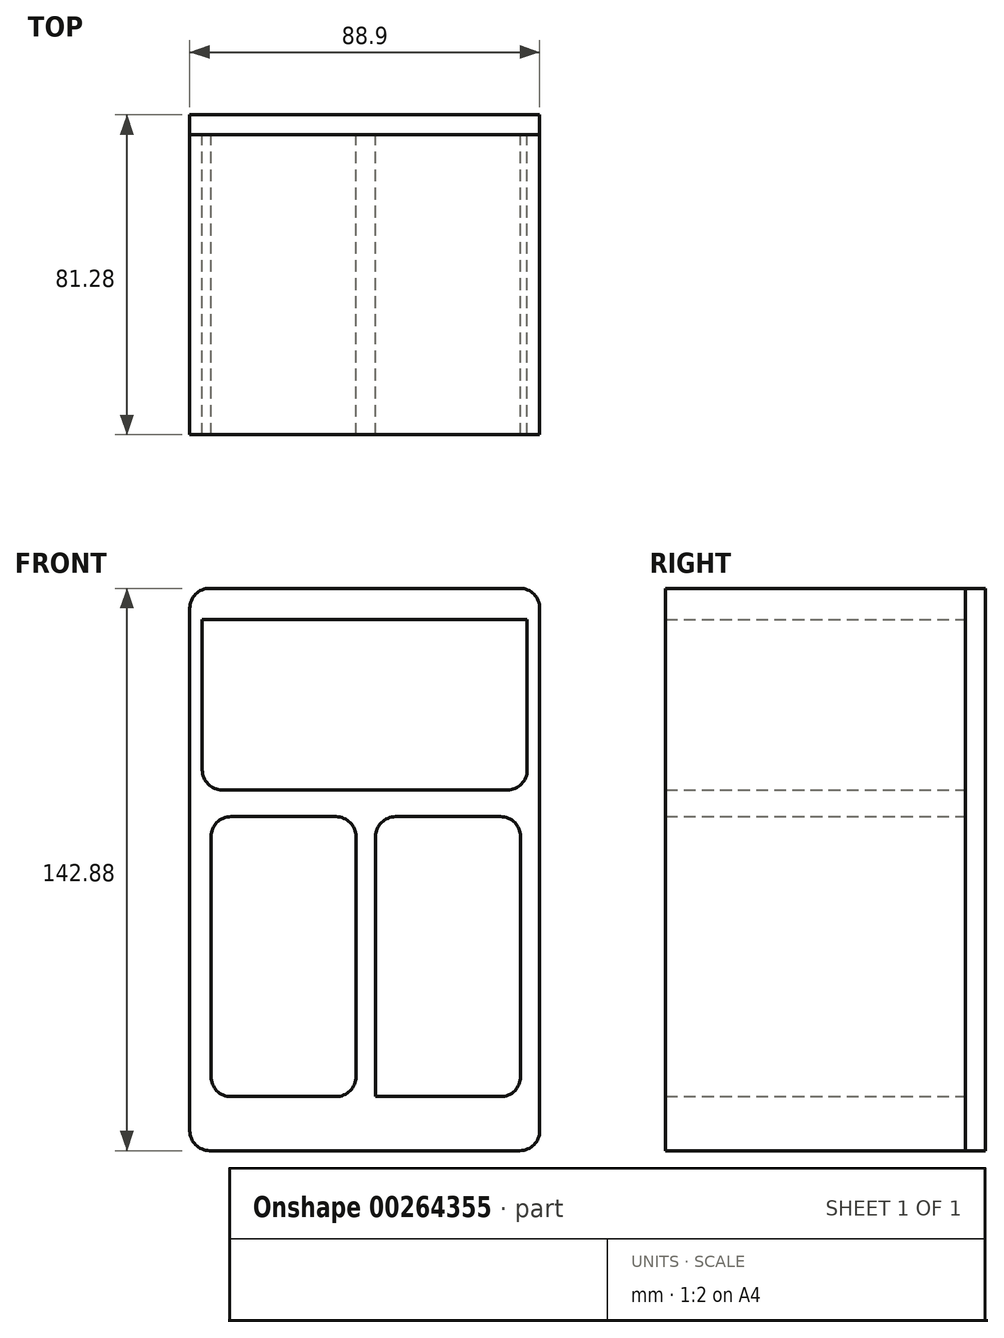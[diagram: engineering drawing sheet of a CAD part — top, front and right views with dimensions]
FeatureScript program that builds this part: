
annotation { "Feature Type Name" : "Feature", "Feature Type Description" : "" }
export const myFeature = defineFeature(function(context is Context, id is Id, definition is map)
    precondition{}
    {
        {
            var Q0;
            Q0=qCreatedBy(makeId("Front.planeOp"),FACE);
            var sketch = newSketch(context, id + "F0", { "sketchPlane" : qUnion([Q0])});
            skLineSegment(sketch, "E0.bottom", {"start": v(-44.45, 71.44) * mm, "end": v(44.45, 71.44) * mm});
            skLineSegment(sketch, "E0.top", {"start": v(-44.45, -71.44) * mm, "end": v(44.45, -71.44) * mm});
            skLineSegment(sketch, "E0.left", {"start": v(-44.45, 71.44) * mm, "end": v(-44.45, -71.44) * mm});
            skLineSegment(sketch, "E0.right", {"start": v(44.45, 71.44) * mm, "end": v(44.45, -71.44) * mm});
            skPoint(sketch, "E0.middle", {"position": v(0, 0) * mm});
            skLineSegment(sketch, "E1.bottom", {"start": v(-41.27, 63.5) * mm, "end": v(41.28, 63.5) * mm});
            skLineSegment(sketch, "E1.top", {"start": v(-41.28, -63.5) * mm, "end": v(41.27, -63.5) * mm});
            skLineSegment(sketch, "E1.left", {"start": v(-41.27, 63.5) * mm, "end": v(-41.28, -63.5) * mm});
            skLineSegment(sketch, "E1.right", {"start": v(41.28, 63.5) * mm, "end": v(41.27, -63.5) * mm});
            skLineSegment(sketch, "E2.bottom", {"start": v(-41.27, 63.5) * mm, "end": v(41.27, 63.5) * mm});
            skLineSegment(sketch, "E2.top", {"start": v(-41.27, 20.2) * mm, "end": v(41.27, 20.2) * mm});
            skLineSegment(sketch, "E2.left", {"start": v(-41.27, 63.5) * mm, "end": v(-41.27, 20.2) * mm});
            skLineSegment(sketch, "E2.right", {"start": v(41.27, 63.5) * mm, "end": v(41.27, 20.2) * mm});
            skPoint(sketch, "E2.middle", {"position": v(0, 41.85) * mm});
            skLineSegment(sketch, "E3.bottom", {"start": v(-39.08, 13.42) * mm, "end": v(-2.25, 13.42) * mm});
            skLineSegment(sketch, "E3.top", {"start": v(-39.08, -57.7) * mm, "end": v(-2.25, -57.7) * mm});
            skLineSegment(sketch, "E3.left", {"start": v(-39.08, 13.42) * mm, "end": v(-39.08, -57.7) * mm});
            skLineSegment(sketch, "E3.right", {"start": v(-2.25, 13.42) * mm, "end": v(-2.25, -57.7) * mm});
            skLineSegment(sketch, "E4.bottom", {"start": v(2.77, 13.42) * mm, "end": v(39.6, 13.42) * mm});
            skLineSegment(sketch, "E4.top", {"start": v(2.77, -57.7) * mm, "end": v(39.6, -57.7) * mm});
            skLineSegment(sketch, "E4.left", {"start": v(2.77, 13.42) * mm, "end": v(2.77, -57.7) * mm});
            skLineSegment(sketch, "E4.right", {"start": v(39.6, 13.42) * mm, "end": v(39.6, -57.7) * mm});
            skSolve(sketch);
        }
        {
            var Q0;
            Q0=makeQuery(id+"F0.imprint","IMPRINT",FACE,{"disambiguationData":[TD([[makeQuery(id+"F0.imprint","IMPRINT",EDGE,{"derivedFrom":sQuery(id+"F0.wireOp",EDGE,"E0.bottom")}),-1.0]])]});
            var Q1;
            Q1=makeQuery(id+"F0.imprint","IMPRINT",FACE,{"disambiguationData":[TD([[makeQuery(id+"F0.imprint","IMPRINT",EDGE,{"derivedFrom":sQuery(id+"F0.wireOp",EDGE,"E1.top")}),1.0]])]});
            extrude(context, id + "F1", {"entities" : qUnion([Q0, Q1]), "depth" : 76.2 * mm});
        }
        {
            var Q0;
            Q0=makeQuery(id+"F1.opExtrude","SWEPT_EDGE",EDGE,{"disambiguationData":[OSD([sQuery(id+"F0.wireOp",EDGE,"E0.bottom"),sQuery(id+"F0.wireOp",EDGE,"E0.right")])]});
            var Q1;
            Q1=makeQuery(id+"F1.opExtrude","SWEPT_EDGE",EDGE,{"disambiguationData":[OSD([sQuery(id+"F0.wireOp",EDGE,"E0.bottom"),sQuery(id+"F0.wireOp",EDGE,"E0.left")])]});
            var Q2;
            Q2=makeQuery(id+"F1.opExtrude","SWEPT_EDGE",EDGE,{"disambiguationData":[OSD([sQuery(id+"F0.wireOp",EDGE,"E1.right"),sQuery(id+"F0.wireOp",EDGE,"E2.top"),sQuery(id+"F0.wireOp",EDGE,"E2.right")])]});
            var Q3;
            Q3=makeQuery(id+"F1.opExtrude","SWEPT_EDGE",EDGE,{"disambiguationData":[OSD([sQuery(id+"F0.wireOp",EDGE,"E1.left"),sQuery(id+"F0.wireOp",EDGE,"E2.top"),sQuery(id+"F0.wireOp",EDGE,"E2.left")])]});
            var Q4;
            Q4=makeQuery(id+"F1.opExtrude","SWEPT_EDGE",EDGE,{"disambiguationData":[OSD([sQuery(id+"F0.wireOp",EDGE,"E3.top"),sQuery(id+"F0.wireOp",EDGE,"E3.left")])]});
            var Q5;
            Q5=makeQuery(id+"F1.opExtrude","SWEPT_EDGE",EDGE,{"disambiguationData":[OSD([sQuery(id+"F0.wireOp",EDGE,"E4.top"),sQuery(id+"F0.wireOp",EDGE,"E4.right")])]});
            var Q6;
            Q6=makeQuery(id+"F1.opExtrude","SWEPT_EDGE",EDGE,{"disambiguationData":[OSD([sQuery(id+"F0.wireOp",EDGE,"E3.top"),sQuery(id+"F0.wireOp",EDGE,"E3.right")])]});
            var Q7;
            Q7=makeQuery(id+"F1.opExtrude","SWEPT_EDGE",EDGE,{"disambiguationData":[OSD([sQuery(id+"F0.wireOp",EDGE,"E3.bottom"),sQuery(id+"F0.wireOp",EDGE,"E3.left")])]});
            var Q8;
            Q8=makeQuery(id+"F1.opExtrude","SWEPT_EDGE",EDGE,{"disambiguationData":[OSD([sQuery(id+"F0.wireOp",EDGE,"E4.bottom"),sQuery(id+"F0.wireOp",EDGE,"E4.left")])]});
            var Q9;
            Q9=makeQuery(id+"F1.opExtrude","SWEPT_EDGE",EDGE,{"disambiguationData":[OSD([sQuery(id+"F0.wireOp",EDGE,"E4.bottom"),sQuery(id+"F0.wireOp",EDGE,"E4.right")])]});
            var Q10;
            Q10=makeQuery(id+"F1.opExtrude","SWEPT_EDGE",EDGE,{"disambiguationData":[OSD([sQuery(id+"F0.wireOp",EDGE,"E3.bottom"),sQuery(id+"F0.wireOp",EDGE,"E3.right")])]});
            var Q11;
            Q11=makeQuery(id+"F1.opExtrude","SWEPT_EDGE",EDGE,{"disambiguationData":[OSD([sQuery(id+"F0.wireOp",EDGE,"E0.top"),sQuery(id+"F0.wireOp",EDGE,"E0.right")])]});
            var Q12;
            Q12=makeQuery(id+"F1.opExtrude","SWEPT_EDGE",EDGE,{"disambiguationData":[OSD([sQuery(id+"F0.wireOp",EDGE,"E0.top"),sQuery(id+"F0.wireOp",EDGE,"E0.left")])]});
            fillet(context, id + "F2", {"entities" : qUnion([Q0, Q1, Q2, Q3, Q4, Q5, Q6, Q7, Q8, Q9, Q10, Q11, Q12]), "radius" : 5.08 * mm, "tangentPropagation" : true, "allowEdgeOverflow" : false});
        }
        {
            var Q0;
            Q0=makeQuery(id+"F0.imprint","IMPRINT",FACE,{"disambiguationData":[TD([[makeQuery(id+"F0.imprint","IMPRINT",EDGE,{"derivedFrom":sQuery(id+"F0.wireOp",EDGE,"E2.bottom")}),-1.0]])]});
            var Q1;
            Q1=makeQuery(id+"F0.imprint","IMPRINT",FACE,{"disambiguationData":[TD([[makeQuery(id+"F0.imprint","IMPRINT",EDGE,{"derivedFrom":sQuery(id+"F0.wireOp",EDGE,"E4.bottom")}),-1.0]])]});
            var Q2;
            Q2=makeQuery(id+"F0.imprint","IMPRINT",FACE,{"disambiguationData":[TD([[makeQuery(id+"F0.imprint","IMPRINT",EDGE,{"derivedFrom":sQuery(id+"F0.wireOp",EDGE,"E3.bottom")}),-1.0]])]});
            var Q3;
            Q3=makeQuery(id+"F0.imprint","IMPRINT",FACE,{"disambiguationData":[TD([[makeQuery(id+"F0.imprint","IMPRINT",EDGE,{"derivedFrom":sQuery(id+"F0.wireOp",EDGE,"E1.top")}),1.0]])]});
            var Q4;
            Q4=makeQuery(id+"F0.imprint","IMPRINT",FACE,{"disambiguationData":[TD([[makeQuery(id+"F0.imprint","IMPRINT",EDGE,{"derivedFrom":sQuery(id+"F0.wireOp",EDGE,"E0.bottom")}),-1.0]])]});
            extrude(context, id + "F3", {"entities" : qUnion([Q0, Q1, Q2, Q3, Q4]), "oppositeDirection" : true, "depth" : 5.08 * mm});
        }
        {
            var Q0;
            Q0=makeQuery(id+"F3.opExtrude","SWEPT_EDGE",EDGE,{"disambiguationData":[OSD([sQuery(id+"F0.wireOp",EDGE,"E0.bottom"),sQuery(id+"F0.wireOp",EDGE,"E0.right")])]});
            var Q1;
            Q1=makeQuery(id+"F3.opExtrude","SWEPT_EDGE",EDGE,{"disambiguationData":[OSD([sQuery(id+"F0.wireOp",EDGE,"E0.bottom"),sQuery(id+"F0.wireOp",EDGE,"E0.left")])]});
            var Q2;
            Q2=makeQuery(id+"F3.opExtrude","SWEPT_EDGE",EDGE,{"disambiguationData":[OSD([sQuery(id+"F0.wireOp",EDGE,"E0.top"),sQuery(id+"F0.wireOp",EDGE,"E0.right")])]});
            var Q3;
            Q3=makeQuery(id+"F3.opExtrude","SWEPT_EDGE",EDGE,{"disambiguationData":[OSD([sQuery(id+"F0.wireOp",EDGE,"E0.top"),sQuery(id+"F0.wireOp",EDGE,"E0.left")])]});
            fillet(context, id + "F4", {"entities" : qUnion([Q0, Q1, Q2, Q3]), "radius" : 5.08 * mm, "tangentPropagation" : true, "allowEdgeOverflow" : false});
        }
    });
